# Revit family: MT-PROTILT AW SGL WITH LOW LITE
name_source: partatom
category: Windows
revit_build: Autodesk Revit 2017 (Build: 20160225_1515(x64)
units: mm (PartAtom-declared; Revit-internal decimal feet)

## family parameters
Always vertical = Yes
Cut with Voids When Loaded = No
Host = Wall
OmniClass Number = 23.30.20.00
OmniClass Title = Windows
Room Calculation Point = No
Shared = No

## types (2) — shared parameters
ANZRC COMPLIANT = YES
DOUBLE GLAZED THICKNESS = 18 mm
Default Sill Height = 900 mm  [stored 2.95276 ft]
FRAME MATERIAL = <By Category>
FRAME THICKNESS = 102 mm
GLAZED MATERIAL = Glass
Height = 1800 mm  [stored 5.90551 ft]
MAX HEIGHT = 2000 mm  [stored 6.56168 ft]
MAX PANEL HEIGHT = 2000 mm  [stored 6.56168 ft]
MAX PANEL WIDTH = 1500 mm
MAX WIDTH = 1500 mm
Manufacturer = ALSPEC
Model = HAWKESBURY TOP HUNG COMMERCIAL SLIDING DOOR
OFFSET = 10 mm  [stored 0.0328084 ft]
OVERALL FRAME HEIGHT = 1800 mm  [stored 5.90551 ft]
OVERALL FRAME WIDTH = 1500 mm
Rough Height = 1800 mm  [stored 5.90551 ft]
Rough Width = 1500 mm
SINGLE GLAZED THICKNESS = 5 mm  [stored 0.0164042 ft]
URL = WWW.ALSPEC.COM.AU
VERSION = 2.1
WARNING = No
Wall Closure = By host
Width = 1500 mm
YEAR = 2019
zero-valued in all types: TOLERANCE

## per-type parameters (varying)
| type | BOT PANEL POSITION | MCATHUR 101.6 | PANEL HEIGHT | PANEL WIDTH | TRANSOM HEIGHT | TRANSOM WIDTH |
| HUNTER EVO | 42 mm  [stored 0.137795 ft] | No | 1000 mm  [stored 3.28084 ft] | 1386 mm  [stored 4.54724 ft] | 758 mm | 1500 mm |
| MCARTHUR 101.6 | 37 mm  [stored 0.121391 ft] | Yes | 1013 mm | 1401 mm | 750 mm  [stored 2.46063 ft] | 1512 mm  [stored 4.96063 ft] |

type visibility flags (boolean, named after types; folded from table):
- HUNTER EVO: Yes: HUNTER EVO
- MCARTHUR 101.6: Yes: (none)

note: [stored X ft] marks values corroborated as IEEE doubles in the binary element streams (Revit-internal decimal feet)

## geometry (parser evidence)
native form markers: Sweep x21
no freeform markers — native parametric forms only
